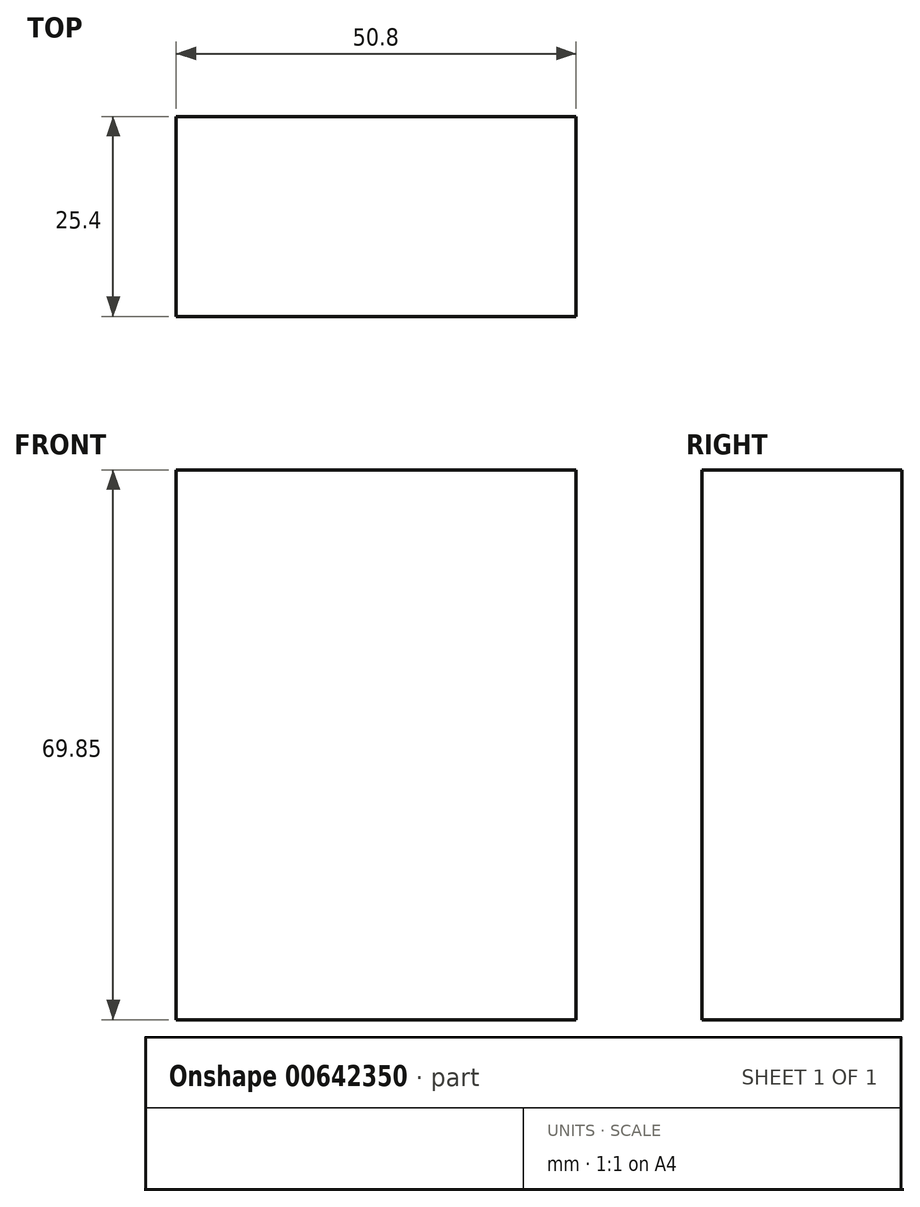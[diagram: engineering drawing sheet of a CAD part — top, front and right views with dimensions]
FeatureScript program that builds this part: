
annotation { "Feature Type Name" : "Feature", "Feature Type Description" : "" }
export const myFeature = defineFeature(function(context is Context, id is Id, definition is map)
    precondition{}
    {
        {
            var Q0;
            Q0=qCreatedBy(makeId("Top.planeOp"),FACE);
            var sketch = newSketch(context, id + "F0", { "sketchPlane" : qUnion([Q0])});
            skLineSegment(sketch, "E0.bottom", {"start": v(-90.33, -45.55) * mm, "end": v(-39.53, -45.55) * mm});
            skLineSegment(sketch, "E0.top", {"start": v(-90.33, -20.15) * mm, "end": v(-39.53, -20.15) * mm});
            skLineSegment(sketch, "E0.left", {"start": v(-90.33, -45.55) * mm, "end": v(-90.33, -20.15) * mm});
            skLineSegment(sketch, "E0.right", {"start": v(-39.53, -45.55) * mm, "end": v(-39.53, -20.15) * mm});
            skSolve(sketch);
        }
        {
            var Q0;
            Q0 = qSketchRegion(id + "F0", true);
            extrude(context, id + "F1", {"entities" : qUnion([Q0]), "depth" : 69.85 * mm, "offsetDistance" : 25.4 * mm});
        }
    });
